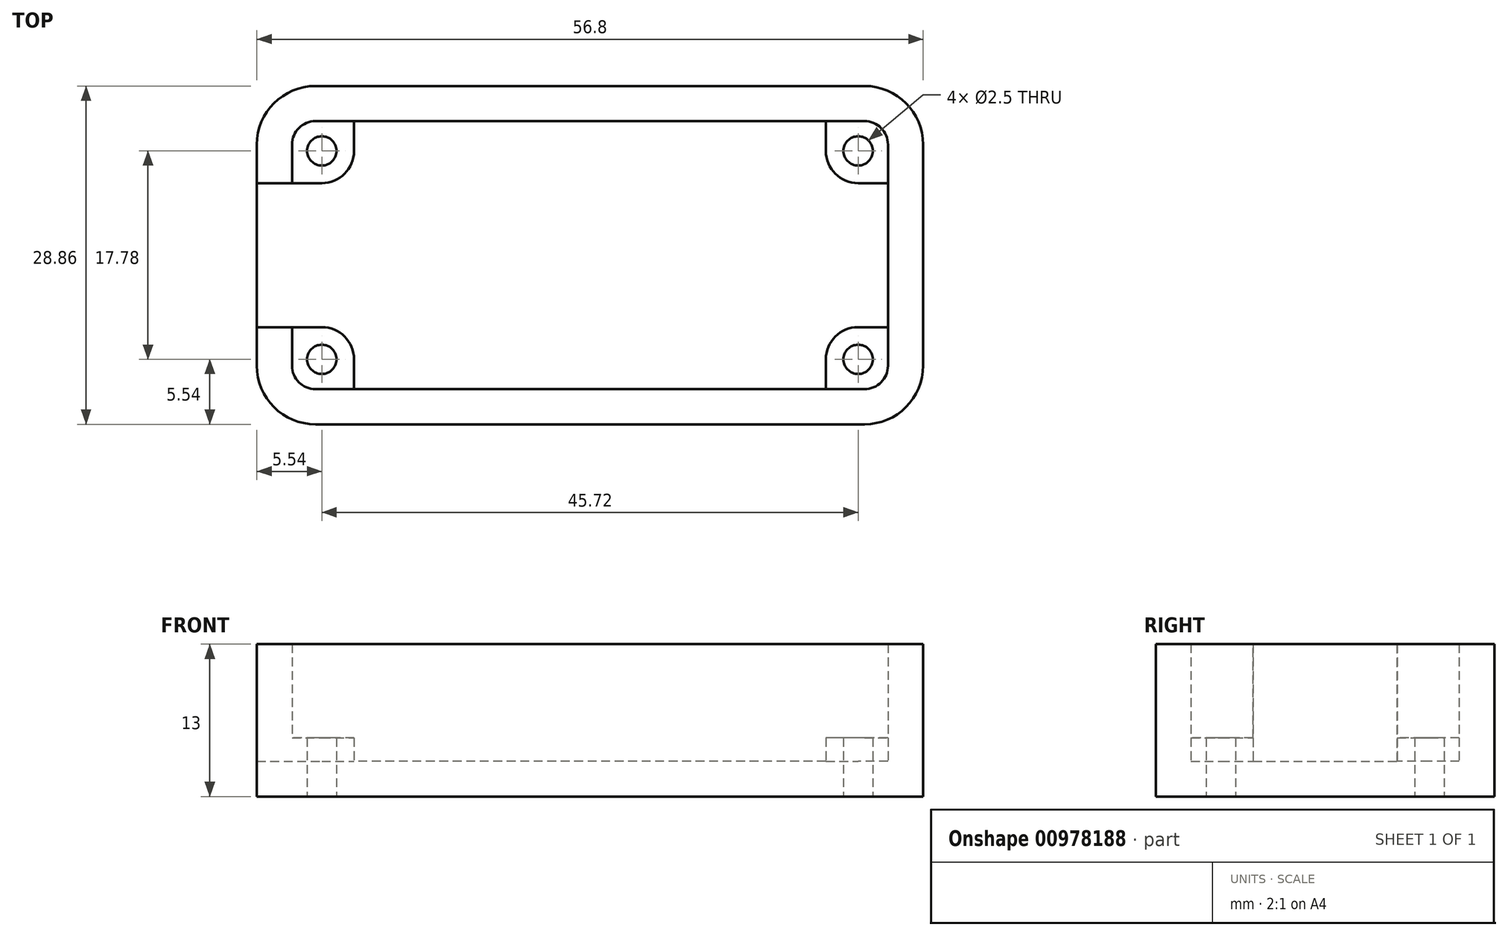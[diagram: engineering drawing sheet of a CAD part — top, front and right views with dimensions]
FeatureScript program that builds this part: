
annotation { "Feature Type Name" : "Feature", "Feature Type Description" : "" }
export const myFeature = defineFeature(function(context is Context, id is Id, definition is map)
    precondition{}
    {
        {
            var Q0;
            Q0=qCreatedBy(makeId("Top.planeOp"),FACE);
            var sketch = newSketch(context, id + "F0", { "sketchPlane" : qUnion([Q0])});
            skLineSegment(sketch, "E0.bottom", {"start": v(-28.4, 14.43) * mm, "end": v(28.4, 14.43) * mm});
            skLineSegment(sketch, "E0.top", {"start": v(-28.4, -14.43) * mm, "end": v(28.4, -14.43) * mm});
            skLineSegment(sketch, "E0.left", {"start": v(-28.4, 14.43) * mm, "end": v(-28.4, -14.43) * mm});
            skLineSegment(sketch, "E0.right", {"start": v(28.4, 14.43) * mm, "end": v(28.4, -14.43) * mm});
            skPoint(sketch, "E0.middle", {"position": v(0, 0) * mm});
            skSolve(sketch);
        }
        {
            var Q0;
            Q0=makeQuery(id+"F0.imprint","IMPRINT",FACE,{"disambiguationData":[TD([[makeQuery(id+"F0.imprint","IMPRINT",EDGE,{"derivedFrom":sQuery(id+"F0.wireOp",EDGE,"E0.bottom")}),-1.0]])]});
            extrude(context, id + "F1", {"entities" : qUnion([Q0]), "depth" : 3 * mm, "offsetDistance" : 25 * mm});
        }
        {
            var Q0;
            Q0=makeQuery(id+"F1.opExtrude","CAP_FACE",FACE,{"disambiguationData":[OSD([sQuery(id+"F0.wireOp",EDGE,"E0.bottom"),sQuery(id+"F0.wireOp",EDGE,"E0.top"),sQuery(id+"F0.wireOp",EDGE,"E0.left"),sQuery(id+"F0.wireOp",EDGE,"E0.right")])],"isStart":false});
            var sketch = newSketch(context, id + "F2", { "sketchPlane" : qUnion([Q0])});
            skLineSegment(sketch, "E1.0", {"start": v(-25.4, 11.43) * mm, "end": v(-25.4, -11.43) * mm});
            skLineSegment(sketch, "E1.1", {"start": v(25.4, 11.43) * mm, "end": v(-25.4, 11.43) * mm});
            skLineSegment(sketch, "E1.2", {"start": v(25.4, -11.43) * mm, "end": v(25.4, 11.43) * mm});
            skLineSegment(sketch, "E1.3", {"start": v(-25.4, -11.43) * mm, "end": v(25.4, -11.43) * mm});
            skSolve(sketch);
        }
        {
            var Q0;
            Q0=makeQuery(id+"F2.imprint","IMPRINT",FACE,{"disambiguationData":[TD([[makeQuery(id+"F2.imprint","IMPRINT",EDGE,{"derivedFrom":sQuery(id+"F2.wireOp",EDGE,"E1.0")}),-1.0]])]});
            extrude(context, id + "F3", {"entities" : qUnion([Q0]), "operationType" : NewBodyOperationType.ADD, "depth" : 10 * mm, "offsetDistance" : 25 * mm});
        }
        {
            var Q0;
            Q0=makeQuery(id+"F1.opExtrude","CAP_FACE",FACE,{"disambiguationData":[OSD([sQuery(id+"F0.wireOp",EDGE,"E0.bottom"),sQuery(id+"F0.wireOp",EDGE,"E0.top"),sQuery(id+"F0.wireOp",EDGE,"E0.left"),sQuery(id+"F0.wireOp",EDGE,"E0.right")])],"isStart":false});
            var sketch = newSketch(context, id + "F4", { "sketchPlane" : qUnion([Q0])});
            skLineSegment(sketch, "E2.bottom", {"start": v(-22.86, 8.89) * mm, "end": v(22.86, 8.89) * mm, "construction": true});
            skLineSegment(sketch, "E2.top", {"start": v(-22.86, -8.89) * mm, "end": v(22.86, -8.89) * mm, "construction": true});
            skLineSegment(sketch, "E2.left", {"start": v(-22.86, 8.89) * mm, "end": v(-22.86, -8.89) * mm, "construction": true});
            skLineSegment(sketch, "E2.right", {"start": v(22.86, 8.89) * mm, "end": v(22.86, -8.89) * mm, "construction": true});
            skPoint(sketch, "E2.middle", {"position": v(0, 0) * mm});
            skCircle(sketch, "E3", {"center": v(-22.86, 8.89) * mm, "radius": 1.25 * mm});
            skCircle(sketch, "E4", {"center": v(-22.86, -8.89) * mm, "radius": 1.25 * mm});
            skCircle(sketch, "E5", {"center": v(22.86, -8.89) * mm, "radius": 1.25 * mm});
            skCircle(sketch, "E6", {"center": v(22.86, 8.89) * mm, "radius": 1.25 * mm});
            skLineSegment(sketch, "E7.bottom", {"start": v(-25.4, 11.43) * mm, "end": v(-20.11, 11.43) * mm});
            skLineSegment(sketch, "E7.top", {"start": v(-25.4, 6.14) * mm, "end": v(-20.11, 6.14) * mm});
            skLineSegment(sketch, "E7.left", {"start": v(-25.4, 11.43) * mm, "end": v(-25.4, 6.14) * mm});
            skLineSegment(sketch, "E7.right", {"start": v(-20.11, 11.43) * mm, "end": v(-20.11, 6.14) * mm});
            skLineSegment(sketch, "E8.bottom", {"start": v(-25.4, -11.43) * mm, "end": v(-20.11, -11.43) * mm});
            skLineSegment(sketch, "E8.top", {"start": v(-25.4, -6.14) * mm, "end": v(-20.11, -6.14) * mm});
            skLineSegment(sketch, "E8.left", {"start": v(-25.4, -11.43) * mm, "end": v(-25.4, -6.14) * mm});
            skLineSegment(sketch, "E8.right", {"start": v(-20.11, -11.43) * mm, "end": v(-20.11, -6.14) * mm});
            skLineSegment(sketch, "E9.bottom", {"start": v(25.4, -11.43) * mm, "end": v(20.1, -11.43) * mm});
            skLineSegment(sketch, "E9.top", {"start": v(25.4, -6.14) * mm, "end": v(20.1, -6.14) * mm});
            skLineSegment(sketch, "E9.left", {"start": v(25.4, -11.43) * mm, "end": v(25.4, -6.14) * mm});
            skLineSegment(sketch, "E9.right", {"start": v(20.1, -11.43) * mm, "end": v(20.1, -6.14) * mm});
            skLineSegment(sketch, "E10.bottom", {"start": v(25.4, 11.43) * mm, "end": v(20.1, 11.43) * mm});
            skLineSegment(sketch, "E10.top", {"start": v(25.4, 6.14) * mm, "end": v(20.1, 6.14) * mm});
            skLineSegment(sketch, "E10.left", {"start": v(25.4, 11.43) * mm, "end": v(25.4, 6.14) * mm});
            skLineSegment(sketch, "E10.right", {"start": v(20.1, 11.43) * mm, "end": v(20.1, 6.14) * mm});
            skSolve(sketch);
        }
        {
            var Q0;
            Q0=makeQuery(id+"F4.imprint","IMPRINT",FACE,{"disambiguationData":[TD([[makeQuery(id+"F4.imprint","IMPRINT",EDGE,{"derivedFrom":sQuery(id+"F4.wireOp",EDGE,"E3")}),-1.0]])]});
            var Q1;
            Q1=makeQuery(id+"F4.imprint","IMPRINT",FACE,{"disambiguationData":[TD([[makeQuery(id+"F4.imprint","IMPRINT",EDGE,{"derivedFrom":sQuery(id+"F4.wireOp",EDGE,"E5")}),-1.0]])]});
            var Q2;
            Q2=makeQuery(id+"F4.imprint","IMPRINT",FACE,{"disambiguationData":[TD([[makeQuery(id+"F4.imprint","IMPRINT",EDGE,{"derivedFrom":sQuery(id+"F4.wireOp",EDGE,"E6")}),-1.0]])]});
            var Q3;
            Q3=makeQuery(id+"F4.imprint","IMPRINT",FACE,{"disambiguationData":[TD([[makeQuery(id+"F4.imprint","IMPRINT",EDGE,{"derivedFrom":sQuery(id+"F4.wireOp",EDGE,"E4")}),-1.0]])]});
            extrude(context, id + "F5", {"entities" : qUnion([Q0, Q1, Q2, Q3]), "operationType" : NewBodyOperationType.ADD, "depth" : 2 * mm, "offsetDistance" : 25 * mm});
        }
        {
            var Q0;
            Q0=makeQuery(id+"F5.opExtrude","SWEPT_EDGE",EDGE,{"disambiguationData":[OSD([sQuery(id+"F4.wireOp",EDGE,"E7.top"),sQuery(id+"F4.wireOp",EDGE,"E7.right")])]});
            var Q1;
            Q1=makeQuery(id+"F5.opExtrude","SWEPT_EDGE",EDGE,{"disambiguationData":[OSD([sQuery(id+"F4.wireOp",EDGE,"E10.top"),sQuery(id+"F4.wireOp",EDGE,"E10.right")])]});
            var Q2;
            Q2=makeQuery(id+"F5.opExtrude","SWEPT_EDGE",EDGE,{"disambiguationData":[OSD([sQuery(id+"F4.wireOp",EDGE,"E9.top"),sQuery(id+"F4.wireOp",EDGE,"E9.right")])]});
            var Q3;
            Q3=makeQuery(id+"F5.opExtrude","SWEPT_EDGE",EDGE,{"disambiguationData":[OSD([sQuery(id+"F4.wireOp",EDGE,"E8.top"),sQuery(id+"F4.wireOp",EDGE,"E8.right")])]});
            fillet(context, id + "F6", {"entities" : qUnion([Q0, Q1, Q2, Q3]), "radius" : (1.5 + 2.5 / 2) * mm, "tangentPropagation" : true, "allowEdgeOverflow" : false});
        }
        {
            var Q0;
            Q0=makeQuery(id+"F3.opExtrude","SWEPT_EDGE",EDGE,{"disambiguationData":[OSD([sQuery(id+"F2.wireOp",EDGE,"E1.0"),sQuery(id+"F2.wireOp",EDGE,"E1.1")])]});
            var Q1;
            Q1=makeQuery(id+"F3.opExtrude","SWEPT_EDGE",EDGE,{"disambiguationData":[OSD([sQuery(id+"F2.wireOp",EDGE,"E1.1"),sQuery(id+"F2.wireOp",EDGE,"E1.2")])]});
            var Q2;
            Q2=makeQuery(id+"F3.opExtrude","SWEPT_EDGE",EDGE,{"disambiguationData":[OSD([sQuery(id+"F2.wireOp",EDGE,"E1.2"),sQuery(id+"F2.wireOp",EDGE,"E1.3")])]});
            var Q3;
            Q3=makeQuery(id+"F3.opExtrude","SWEPT_EDGE",EDGE,{"disambiguationData":[OSD([sQuery(id+"F2.wireOp",EDGE,"E1.0"),sQuery(id+"F2.wireOp",EDGE,"E1.3")])]});
            fillet(context, id + "F7", {"entities" : qUnion([Q0, Q1, Q2, Q3]), "radius" : 2 * mm, "tangentPropagation" : true, "allowEdgeOverflow" : false});
        }
        {
            var Q0;
            {var subQ0=sQuery(id+"F0.wireOp",EDGE,"E0.right");var subQ1=sQuery(id+"F0.wireOp",EDGE,"E0.bottom");Q0=makeQuery(id+"F3.boolean.opBoolean","MERGE",EDGE,{"derivedFrom":[makeQuery(id+"F1.opExtrude","SWEPT_EDGE",EDGE,{"disambiguationData":[OSD([subQ1,subQ0])]}),makeQuery(id+"F3.opExtrude","SWEPT_EDGE",EDGE,{"disambiguationData":[OSD([subQ1,subQ0])]})]});}
            var Q1;
            {var subQ0=sQuery(id+"F0.wireOp",EDGE,"E0.right");var subQ1=sQuery(id+"F0.wireOp",EDGE,"E0.top");Q1=makeQuery(id+"F3.boolean.opBoolean","MERGE",EDGE,{"derivedFrom":[makeQuery(id+"F1.opExtrude","SWEPT_EDGE",EDGE,{"disambiguationData":[OSD([subQ1,subQ0])]}),makeQuery(id+"F3.opExtrude","SWEPT_EDGE",EDGE,{"disambiguationData":[OSD([subQ1,subQ0])]})]});}
            var Q2;
            {var subQ0=sQuery(id+"F0.wireOp",EDGE,"E0.left");var subQ1=sQuery(id+"F0.wireOp",EDGE,"E0.top");Q2=makeQuery(id+"F3.boolean.opBoolean","MERGE",EDGE,{"derivedFrom":[makeQuery(id+"F1.opExtrude","SWEPT_EDGE",EDGE,{"disambiguationData":[OSD([subQ1,subQ0])]}),makeQuery(id+"F3.opExtrude","SWEPT_EDGE",EDGE,{"disambiguationData":[OSD([subQ1,subQ0])]})]});}
            var Q3;
            {var subQ0=sQuery(id+"F0.wireOp",EDGE,"E0.left");var subQ1=sQuery(id+"F0.wireOp",EDGE,"E0.bottom");Q3=makeQuery(id+"F3.boolean.opBoolean","MERGE",EDGE,{"derivedFrom":[makeQuery(id+"F1.opExtrude","SWEPT_EDGE",EDGE,{"disambiguationData":[OSD([subQ1,subQ0])]}),makeQuery(id+"F3.opExtrude","SWEPT_EDGE",EDGE,{"disambiguationData":[OSD([subQ1,subQ0])]})]});}
            fillet(context, id + "F8", {"entities" : qUnion([Q0, Q1, Q2, Q3]), "radius" : 5 * mm, "tangentPropagation" : true, "allowEdgeOverflow" : false});
        }
        {
            var Q0;
            Q0=makeQuery(id+"F3.opExtrude","SWEPT_FACE",FACE,{"disambiguationData":[OSD([sQuery(id+"F2.wireOp",EDGE,"E1.0")])]});
            var sketch = newSketch(context, id + "F9", { "sketchPlane" : qUnion([Q0])});
            skPoint(sketch, "E11.oppositeSnap0", {"position": v(-6.14, 4) * mm});
            skLineSegment(sketch, "E11.bottom", {"start": v(6.14, 3) * mm, "end": v(-6.14, 3) * mm});
            skLineSegment(sketch, "E11.top", {"start": v(6.14, 13) * mm, "end": v(-6.14, 13) * mm});
            skLineSegment(sketch, "E11.left", {"start": v(6.14, 3) * mm, "end": v(6.14, 13) * mm});
            skLineSegment(sketch, "E11.right", {"start": v(-6.14, 3) * mm, "end": v(-6.14, 13) * mm});
            skSolve(sketch);
        }
        {
            var Q0;
            Q0 = qSketchRegion(id + "F9", true);
            extrude(context, id + "F10", {"entities" : qUnion([Q0]), "operationType" : NewBodyOperationType.REMOVE, "endBound" : BoundingType.UP_TO_NEXT, "oppositeDirection" : true, "depth" : 25 * mm, "offsetDistance" : 25 * mm});
        }
        {
            var Q0;
            Q0=makeQuery(id+"F5.boolean.opBoolean","SPLIT",FACE,{"disambiguationData":[TD([makeQuery(id+"F5.opExtrude","SWEPT_FACE",FACE,{"disambiguationData":[OSD([sQuery(id+"F4.wireOp",EDGE,"E6")])]})])],"derivedFrom":makeQuery(id+"F1.opExtrude","CAP_FACE",FACE,{"disambiguationData":[OSD([sQuery(id+"F0.wireOp",EDGE,"E0.bottom"),sQuery(id+"F0.wireOp",EDGE,"E0.top"),sQuery(id+"F0.wireOp",EDGE,"E0.left"),sQuery(id+"F0.wireOp",EDGE,"E0.right")])],"isStart":false})});
            var Q1;
            Q1=makeQuery(id+"F5.boolean.opBoolean","SPLIT",FACE,{"disambiguationData":[TD([makeQuery(id+"F5.opExtrude","SWEPT_FACE",FACE,{"disambiguationData":[OSD([sQuery(id+"F4.wireOp",EDGE,"E5")])]})])],"derivedFrom":makeQuery(id+"F1.opExtrude","CAP_FACE",FACE,{"disambiguationData":[OSD([sQuery(id+"F0.wireOp",EDGE,"E0.bottom"),sQuery(id+"F0.wireOp",EDGE,"E0.top"),sQuery(id+"F0.wireOp",EDGE,"E0.left"),sQuery(id+"F0.wireOp",EDGE,"E0.right")])],"isStart":false})});
            var Q2;
            Q2=makeQuery(id+"F5.boolean.opBoolean","SPLIT",FACE,{"disambiguationData":[TD([makeQuery(id+"F5.opExtrude","SWEPT_FACE",FACE,{"disambiguationData":[OSD([sQuery(id+"F4.wireOp",EDGE,"E4")])]})])],"derivedFrom":makeQuery(id+"F1.opExtrude","CAP_FACE",FACE,{"disambiguationData":[OSD([sQuery(id+"F0.wireOp",EDGE,"E0.bottom"),sQuery(id+"F0.wireOp",EDGE,"E0.top"),sQuery(id+"F0.wireOp",EDGE,"E0.left"),sQuery(id+"F0.wireOp",EDGE,"E0.right")])],"isStart":false})});
            var Q3;
            Q3=makeQuery(id+"F5.boolean.opBoolean","SPLIT",FACE,{"disambiguationData":[TD([makeQuery(id+"F5.opExtrude","SWEPT_FACE",FACE,{"disambiguationData":[OSD([sQuery(id+"F4.wireOp",EDGE,"E3")])]})])],"derivedFrom":makeQuery(id+"F1.opExtrude","CAP_FACE",FACE,{"disambiguationData":[OSD([sQuery(id+"F0.wireOp",EDGE,"E0.bottom"),sQuery(id+"F0.wireOp",EDGE,"E0.top"),sQuery(id+"F0.wireOp",EDGE,"E0.left"),sQuery(id+"F0.wireOp",EDGE,"E0.right")])],"isStart":false})});
            extrude(context, id + "F11", {"entities" : qUnion([Q0, Q1, Q2, Q3]), "operationType" : NewBodyOperationType.REMOVE, "endBound" : BoundingType.UP_TO_NEXT, "oppositeDirection" : true, "depth" : 25 * mm, "offsetDistance" : 25 * mm});
        }
    });
